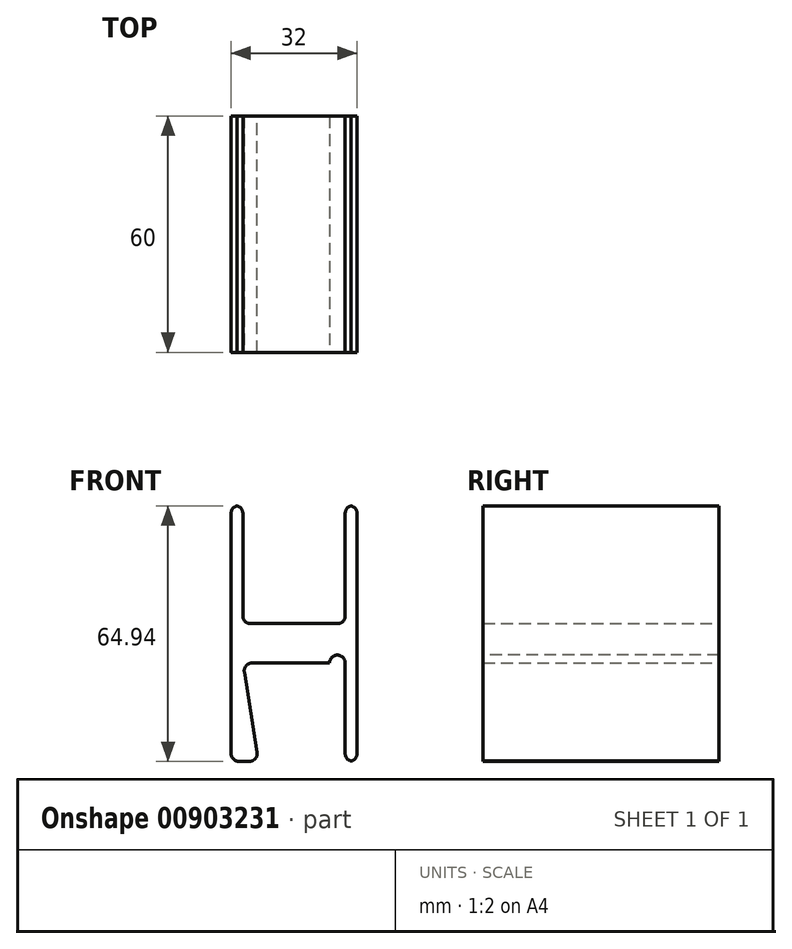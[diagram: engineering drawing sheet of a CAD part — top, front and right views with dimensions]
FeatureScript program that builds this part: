
annotation { "Feature Type Name" : "Feature", "Feature Type Description" : "" }
export const myFeature = defineFeature(function(context is Context, id is Id, definition is map)
    precondition{}
    {
        {
            var Q0;
            Q0=qCreatedBy(makeId("Front.planeOp"),FACE);
            var sketch = newSketch(context, id + "F0", { "sketchPlane" : qUnion([Q0])});
            skLineSegment(sketch, "E0", {"start": v(16, -25) * mm, "end": v(16, 10) * mm});
            skLineSegment(sketch, "E1", {"start": v(16, 10) * mm, "end": v(-16, 10) * mm});
            skLineSegment(sketch, "E2", {"start": v(-16, 10) * mm, "end": v(-16, -25) * mm});
            skLineSegment(sketch, "E3", {"start": v(-16, -25) * mm, "end": v(-9, -25) * mm});
            skLineSegment(sketch, "E4", {"start": v(-9, -25) * mm, "end": v(-13, 0) * mm});
            skLineSegment(sketch, "E5", {"start": v(-13, 0) * mm, "end": v(13, 0) * mm});
            skLineSegment(sketch, "E6", {"start": v(13, 0) * mm, "end": v(13, -25) * mm});
            skLineSegment(sketch, "E7", {"start": v(13, -25) * mm, "end": v(16, -25) * mm});
            skLineSegment(sketch, "E8.bottom", {"start": v(16, 10) * mm, "end": v(13, 10) * mm});
            skLineSegment(sketch, "E8.top", {"start": v(16, 40) * mm, "end": v(13, 40) * mm});
            skLineSegment(sketch, "E8.left", {"start": v(16, 10) * mm, "end": v(16, 40) * mm});
            skLineSegment(sketch, "E8.right", {"start": v(13, 10) * mm, "end": v(13, 40) * mm});
            skLineSegment(sketch, "E9.bottom", {"start": v(-16, 10) * mm, "end": v(-13, 10) * mm});
            skLineSegment(sketch, "E9.top", {"start": v(-16, 40) * mm, "end": v(-13, 40) * mm});
            skLineSegment(sketch, "E9.left", {"start": v(-16, 10) * mm, "end": v(-16, 40) * mm});
            skLineSegment(sketch, "E9.right", {"start": v(-13, 10) * mm, "end": v(-13, 40) * mm});
            skSolve(sketch);
        }
        {
            var Q0;
            {var subQ3=sQuery(id+"F0.wireOp",EDGE,"E0");Q0=makeQuery(id+"F0.imprint","IMPRINT",FACE,{"disambiguationData":[TD([[makeQuery(id+"F0.imprint","IMPRINT",EDGE,{"derivedFrom":subQ3}),1.0]])]});}
            var Q1;
            Q1=makeQuery(id+"F0.imprint","IMPRINT",FACE,{"disambiguationData":[TD([[makeQuery(id+"F0.imprint","IMPRINT",EDGE,{"derivedFrom":sQuery(id+"F0.wireOp",EDGE,"E9.top")}),-1.0]])]});
            var Q2;
            Q2=makeQuery(id+"F0.imprint","IMPRINT",FACE,{"disambiguationData":[TD([[makeQuery(id+"F0.imprint","IMPRINT",EDGE,{"derivedFrom":sQuery(id+"F0.wireOp",EDGE,"E8.top")}),1.0]])]});
            extrude(context, id + "F1", {"entities" : qUnion([Q0, Q1, Q2]), "endBound" : BoundingType.SYMMETRIC, "depth" : 60 * mm, "offsetDistance" : 25 * mm});
        }
        {
            var Q0;
            Q0=makeQuery(id+"F1.opExtrude","CAP_FACE",FACE,{"disambiguationData":[OSD([sQuery(id+"F0.wireOp",EDGE,"E0"),sQuery(id+"F0.wireOp",EDGE,"E1"),sQuery(id+"F0.wireOp",EDGE,"E2"),sQuery(id+"F0.wireOp",EDGE,"E3"),sQuery(id+"F0.wireOp",EDGE,"E4"),sQuery(id+"F0.wireOp",EDGE,"E5"),sQuery(id+"F0.wireOp",EDGE,"E6"),sQuery(id+"F0.wireOp",EDGE,"E7"),sQuery(id+"F0.wireOp",EDGE,"E8.top"),sQuery(id+"F0.wireOp",EDGE,"E8.left"),sQuery(id+"F0.wireOp",EDGE,"E8.right"),sQuery(id+"F0.wireOp",EDGE,"E9.top"),sQuery(id+"F0.wireOp",EDGE,"E9.left"),sQuery(id+"F0.wireOp",EDGE,"E9.right")])],"isStart":false});
            var sketch = newSketch(context, id + "F2", { "sketchPlane" : qUnion([Q0])});
            skArc(sketch, "E10", {"start": v(13, 0) * mm, "mid": v(11, 2) * mm, "end": v(9, 0) * mm});
            skSolve(sketch);
        }
        {
            var Q0;
            {var subQ0=sQuery(id+"F2.wireOp",EDGE,"E10");Q0=makeQuery(id+"F2.imprint","IMPRINT",FACE,{"disambiguationData":[TD([[makeQuery(id+"F2.imprint","IMPRINT",EDGE,{"derivedFrom":subQ0}),1.0]])]});}
            var Q1;
            Q1=makeQuery(id+"F1.opExtrude","CAP_FACE",FACE,{"disambiguationData":[OSD([sQuery(id+"F0.wireOp",EDGE,"E0"),sQuery(id+"F0.wireOp",EDGE,"E1"),sQuery(id+"F0.wireOp",EDGE,"E2"),sQuery(id+"F0.wireOp",EDGE,"E3"),sQuery(id+"F0.wireOp",EDGE,"E4"),sQuery(id+"F0.wireOp",EDGE,"E5"),sQuery(id+"F0.wireOp",EDGE,"E6"),sQuery(id+"F0.wireOp",EDGE,"E7"),sQuery(id+"F0.wireOp",EDGE,"E8.top"),sQuery(id+"F0.wireOp",EDGE,"E8.left"),sQuery(id+"F0.wireOp",EDGE,"E8.right"),sQuery(id+"F0.wireOp",EDGE,"E9.top"),sQuery(id+"F0.wireOp",EDGE,"E9.left"),sQuery(id+"F0.wireOp",EDGE,"E9.right")])],"isStart":true});
            extrude(context, id + "F3", {"entities" : qUnion([Q0]), "operationType" : NewBodyOperationType.REMOVE, "endBound" : BoundingType.UP_TO_SURFACE, "oppositeDirection" : true, "depth" : 25 * mm, "endBoundEntityFace" : qUnion([Q1]), "offsetDistance" : 25 * mm});
        }
        {
            var Q0;
            Q0=makeQuery(id+"F1.opExtrude","SWEPT_EDGE",EDGE,{"disambiguationData":[OSD([sQuery(id+"F0.wireOp",EDGE,"E3"),sQuery(id+"F0.wireOp",EDGE,"E4")])]});
            var Q1;
            Q1=makeQuery(id+"F1.opExtrude","SWEPT_EDGE",EDGE,{"disambiguationData":[OSD([sQuery(id+"F0.wireOp",EDGE,"E2"),sQuery(id+"F0.wireOp",EDGE,"E3")])]});
            var Q2;
            Q2=makeQuery(id+"F1.opExtrude","SWEPT_EDGE",EDGE,{"disambiguationData":[OSD([sQuery(id+"F0.wireOp",EDGE,"E4"),sQuery(id+"F0.wireOp",EDGE,"E5")])]});
            var Q3;
            Q3=makeQuery(id+"F3.boolean.opBoolean","COPY",EDGE,{"derivedFrom":makeQuery(id+"F3.opExtrude","SWEPT_EDGE",EDGE,{"disambiguationData":[OSD([sQuery(id+"F0.wireOp",EDGE,"E5"),sQuery(id+"F2.wireOp",EDGE,"E10")])]})});
            var Q4;
            Q4=makeQuery(id+"F1.opExtrude","SWEPT_EDGE",EDGE,{"disambiguationData":[OSD([sQuery(id+"F0.wireOp",EDGE,"E0"),sQuery(id+"F0.wireOp",EDGE,"E7")])]});
            var Q5;
            Q5=makeQuery(id+"F1.opExtrude","SWEPT_EDGE",EDGE,{"disambiguationData":[OSD([sQuery(id+"F0.wireOp",EDGE,"E1"),sQuery(id+"F0.wireOp",EDGE,"E9.right")])]});
            var Q6;
            Q6=makeQuery(id+"F1.opExtrude","SWEPT_EDGE",EDGE,{"disambiguationData":[OSD([sQuery(id+"F0.wireOp",EDGE,"E1"),sQuery(id+"F0.wireOp",EDGE,"E8.right")])]});
            var Q7;
            Q7=makeQuery(id+"F1.opExtrude","SWEPT_EDGE",EDGE,{"disambiguationData":[OSD([sQuery(id+"F0.wireOp",EDGE,"E9.top"),sQuery(id+"F0.wireOp",EDGE,"E9.right")])]});
            var Q8;
            Q8=makeQuery(id+"F1.opExtrude","SWEPT_EDGE",EDGE,{"disambiguationData":[OSD([sQuery(id+"F0.wireOp",EDGE,"E9.top"),sQuery(id+"F0.wireOp",EDGE,"E9.left")])]});
            var Q9;
            Q9=makeQuery(id+"F1.opExtrude","SWEPT_EDGE",EDGE,{"disambiguationData":[OSD([sQuery(id+"F0.wireOp",EDGE,"E8.top"),sQuery(id+"F0.wireOp",EDGE,"E8.left")])]});
            var Q10;
            Q10=makeQuery(id+"F1.opExtrude","SWEPT_EDGE",EDGE,{"disambiguationData":[OSD([sQuery(id+"F0.wireOp",EDGE,"E8.top"),sQuery(id+"F0.wireOp",EDGE,"E8.right")])]});
            var Q11;
            Q11=makeQuery(id+"F1.opExtrude","SWEPT_EDGE",EDGE,{"disambiguationData":[OSD([sQuery(id+"F0.wireOp",EDGE,"E6"),sQuery(id+"F0.wireOp",EDGE,"E7")])]});
            fillet(context, id + "F4", {"entities" : qUnion([Q0, Q1, Q2, Q3, Q4, Q5, Q6, Q7, Q8, Q9, Q10, Q11]), "radius" : 2 * mm, "tangentPropagation" : true, "allowEdgeOverflow" : false});
        }
    });
